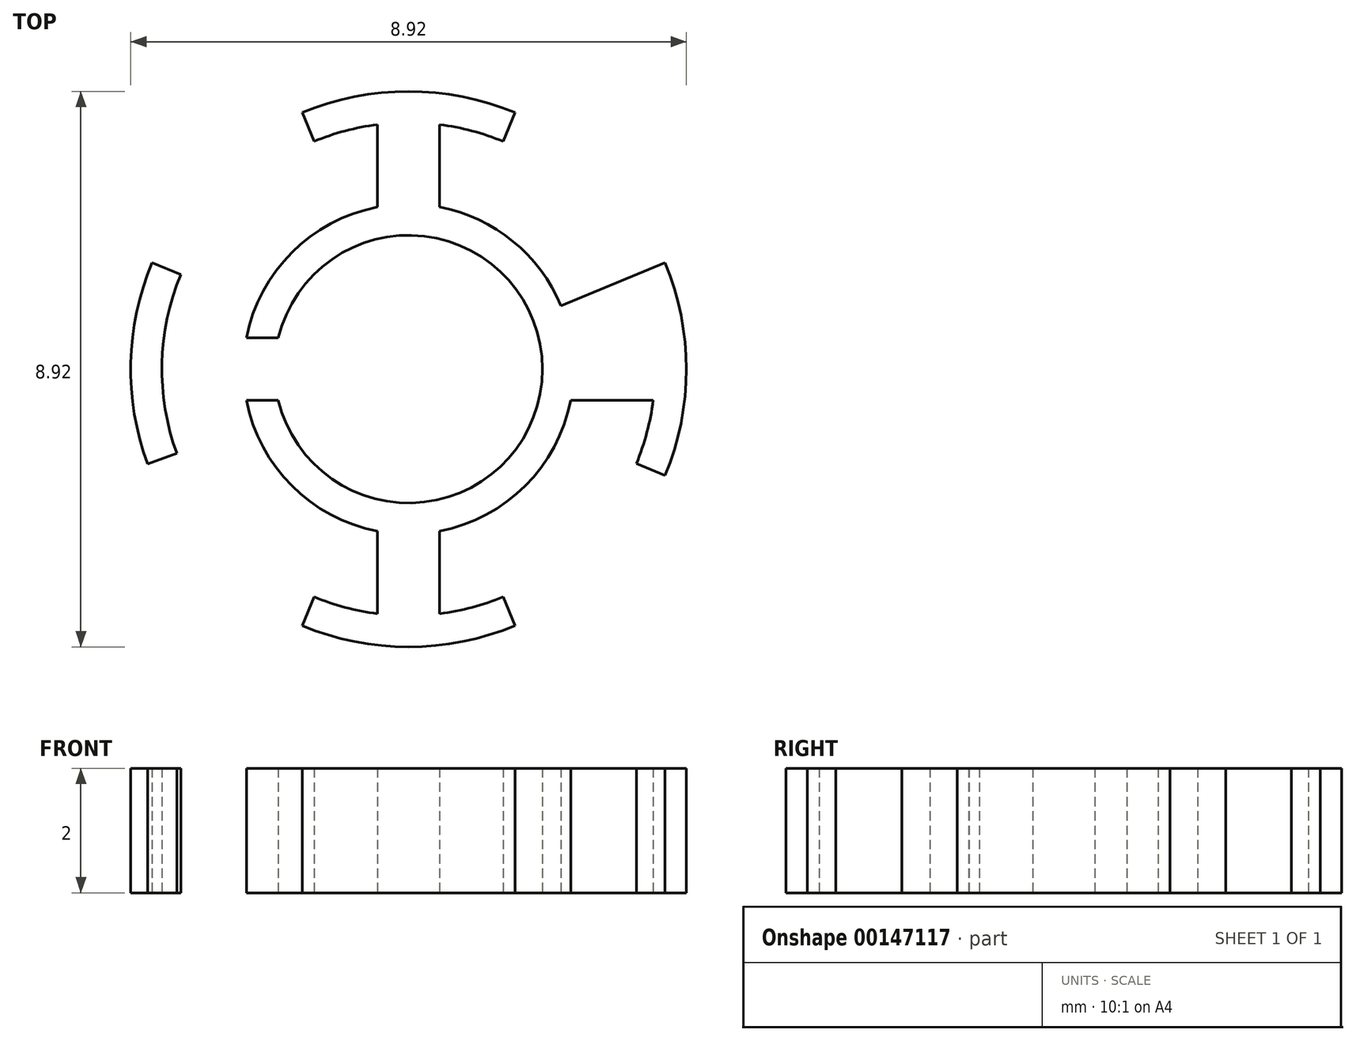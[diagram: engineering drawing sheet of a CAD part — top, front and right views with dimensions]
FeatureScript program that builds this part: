
annotation { "Feature Type Name" : "Feature", "Feature Type Description" : "" }
export const myFeature = defineFeature(function(context is Context, id is Id, definition is map)
    precondition{}
    {
        {
            var Q0;
            Q0=qCreatedBy(makeId("Top.planeOp"),FACE);
            var sketch = newSketch(context, id + "F0", { "sketchPlane" : qUnion([Q0])});
            skCircle(sketch, "E0", {"center": v(0, 0) * mm, "radius": 2.15 * mm});
            skCircle(sketch, "E1", {"center": v(0, 0) * mm, "radius": 2.65 * mm});
            skLineSegment(sketch, "E2", {"start": v(0, 0) * mm, "end": v(0.5, 0) * mm});
            skLineSegment(sketch, "E3", {"start": v(0.5, 0) * mm, "end": v(-0.5, 0) * mm});
            skCircle(sketch, "E4", {"center": v(0, 0) * mm, "radius": 4.46 * mm});
            skCircle(sketch, "E5", {"center": v(0, 0) * mm, "radius": 3.96 * mm});
            skLineSegment(sketch, "E6", {"start": v(-0.5, 0) * mm, "end": v(-0.5, 3.93) * mm});
            skLineSegment(sketch, "E7", {"start": v(0.5, 0) * mm, "end": v(0.5, 3.93) * mm});
            skLineSegment(sketch, "E8", {"start": v(0, 0) * mm, "end": v(0, 4.46) * mm});
            skLineSegment(sketch, "E9", {"start": v(0, 0) * mm, "end": v(1.7, 4.12) * mm});
            skLineSegment(sketch, "E10.MirrorCS", {"start": v(0, 0) * mm, "end": v(-1.7, 4.12) * mm});
            skLineSegment(sketch, "E11.MirrorCS", {"start": v(0, 0) * mm, "end": v(1.7, -4.12) * mm});
            skLineSegment(sketch, "E12.MirrorCS", {"start": v(0, 0) * mm, "end": v(-1.7, -4.12) * mm});
            skLineSegment(sketch, "E13.MirrorCS", {"start": v(0.5, 0) * mm, "end": v(0.5, -3.93) * mm});
            skLineSegment(sketch, "E14.MirrorCS", {"start": v(-0.5, 0) * mm, "end": v(-0.5, -3.93) * mm});
            skLineSegment(sketch, "E15", {"start": v(0, 0) * mm, "end": v(4.12, -1.7) * mm});
            skLineSegment(sketch, "E16", {"start": v(0, 0) * mm, "end": v(4.12, 1.7) * mm});
            skLineSegment(sketch, "E17", {"start": v(0, 0) * mm, "end": v(-4.2, -1.52) * mm});
            skLineSegment(sketch, "E18", {"start": v(0, 0) * mm, "end": v(-4.12, 1.7) * mm});
            skLineSegment(sketch, "E19", {"start": v(0, 0) * mm, "end": v(0, -0.5) * mm});
            skLineSegment(sketch, "E20", {"start": v(0, -0.5) * mm, "end": v(-3.93, -0.5) * mm});
            skLineSegment(sketch, "E21", {"start": v(0, -0.5) * mm, "end": v(0, 0.5) * mm});
            skLineSegment(sketch, "E22", {"start": v(0, 0.5) * mm, "end": v(-3.93, 0.5) * mm});
            skLineSegment(sketch, "E23", {"start": v(-3.93, 0.5) * mm, "end": v(3.93, 0.5) * mm});
            skLineSegment(sketch, "E24", {"start": v(0, -0.5) * mm, "end": v(3.93, -0.5) * mm});
            skSolve(sketch);
        }
        {
            var Q0;
            {var subQ0=sQuery(id+"F0.wireOp",EDGE,"E8");var subQ1=sQuery(id+"F0.wireOp",EDGE,"E4");var subQ2=makeQuery(id+"F0.imprint","INTERSECT",VERTEX,{"derivedFrom":[subQ1,subQ0]});Q0=makeQuery(id+"F0.imprint","IMPRINT",FACE,{"disambiguationData":[TD([[makeQuery(id+"F0.imprint","IMPRINT",EDGE,{"disambiguationData":[TD([[subQ2,1.0]])],"derivedFrom":subQ1}),1.0]])]});}
            var Q1;
            {var subQ0=sQuery(id+"F0.wireOp",EDGE,"E8");var subQ1=sQuery(id+"F0.wireOp",EDGE,"E4");var subQ2=makeQuery(id+"F0.imprint","INTERSECT",VERTEX,{"derivedFrom":[subQ1,subQ0]});Q1=makeQuery(id+"F0.imprint","IMPRINT",FACE,{"disambiguationData":[TD([[makeQuery(id+"F0.imprint","IMPRINT",EDGE,{"disambiguationData":[TD([[subQ2,-1.0]])],"derivedFrom":subQ1}),1.0]])]});}
            var Q2;
            {var subQ0=sQuery(id+"F0.wireOp",EDGE,"E8");var subQ1=sQuery(id+"F0.wireOp",EDGE,"E1");var subQ2=makeQuery(id+"F0.imprint","INTERSECT",VERTEX,{"derivedFrom":[subQ1,subQ0]});Q2=makeQuery(id+"F0.imprint","IMPRINT",FACE,{"disambiguationData":[TD([[makeQuery(id+"F0.imprint","IMPRINT",EDGE,{"disambiguationData":[TD([[subQ2,-1.0]])],"derivedFrom":subQ1}),-1.0]])]});}
            var Q3;
            {var subQ0=sQuery(id+"F0.wireOp",EDGE,"E7");var subQ1=sQuery(id+"F0.wireOp",EDGE,"E1");var subQ2=makeQuery(id+"F0.imprint","INTERSECT",VERTEX,{"derivedFrom":[subQ1,subQ0]});Q3=makeQuery(id+"F0.imprint","IMPRINT",FACE,{"disambiguationData":[TD([[makeQuery(id+"F0.imprint","IMPRINT",EDGE,{"disambiguationData":[TD([[subQ2,-1.0]])],"derivedFrom":subQ1}),-1.0]])]});}
            var Q4;
            {var subQ0=sQuery(id+"F0.wireOp",EDGE,"E7");var subQ1=sQuery(id+"F0.wireOp",EDGE,"E0");var subQ2=makeQuery(id+"F0.imprint","INTERSECT",VERTEX,{"derivedFrom":[subQ1,subQ0]});Q4=makeQuery(id+"F0.imprint","IMPRINT",FACE,{"disambiguationData":[TD([[makeQuery(id+"F0.imprint","IMPRINT",EDGE,{"disambiguationData":[TD([[subQ2,-1.0]])],"derivedFrom":subQ1}),-1.0]])]});}
            var Q5;
            {var subQ0=sQuery(id+"F0.wireOp",EDGE,"E8");var subQ1=sQuery(id+"F0.wireOp",EDGE,"E0");var subQ2=makeQuery(id+"F0.imprint","INTERSECT",VERTEX,{"derivedFrom":[subQ1,subQ0]});Q5=makeQuery(id+"F0.imprint","IMPRINT",FACE,{"disambiguationData":[TD([[makeQuery(id+"F0.imprint","IMPRINT",EDGE,{"disambiguationData":[TD([[subQ2,-1.0]])],"derivedFrom":subQ1}),-1.0]])]});}
            var Q6;
            {var subQ0=sQuery(id+"F0.wireOp",EDGE,"E6");var subQ1=sQuery(id+"F0.wireOp",EDGE,"E0");var subQ2=makeQuery(id+"F0.imprint","INTERSECT",VERTEX,{"derivedFrom":[subQ1,subQ0]});Q6=makeQuery(id+"F0.imprint","IMPRINT",FACE,{"disambiguationData":[TD([[makeQuery(id+"F0.imprint","IMPRINT",EDGE,{"disambiguationData":[TD([[subQ2,-1.0]])],"derivedFrom":subQ1}),-1.0]])]});}
            var Q7;
            {var subQ0=sQuery(id+"F0.wireOp",EDGE,"E7");var subQ1=sQuery(id+"F0.wireOp",EDGE,"E0");var subQ2=makeQuery(id+"F0.imprint","INTERSECT",VERTEX,{"derivedFrom":[subQ1,subQ0]});Q7=makeQuery(id+"F0.imprint","IMPRINT",FACE,{"disambiguationData":[TD([[makeQuery(id+"F0.imprint","IMPRINT",EDGE,{"disambiguationData":[TD([[subQ2,1.0]])],"derivedFrom":subQ1}),-1.0]])]});}
            var Q8;
            {var subQ0=sQuery(id+"F0.wireOp",EDGE,"E9");var subQ1=sQuery(id+"F0.wireOp",EDGE,"E0");var subQ2=makeQuery(id+"F0.imprint","INTERSECT",VERTEX,{"derivedFrom":[subQ1,subQ0]});Q8=makeQuery(id+"F0.imprint","IMPRINT",FACE,{"disambiguationData":[TD([[makeQuery(id+"F0.imprint","IMPRINT",EDGE,{"disambiguationData":[TD([[subQ2,1.0]])],"derivedFrom":subQ1}),-1.0]])]});}
            var Q9;
            {var subQ0=sQuery(id+"F0.wireOp",EDGE,"E10.MirrorCS");var subQ1=sQuery(id+"F0.wireOp",EDGE,"E0");var subQ2=makeQuery(id+"F0.imprint","INTERSECT",VERTEX,{"derivedFrom":[subQ1,subQ0]});Q9=makeQuery(id+"F0.imprint","IMPRINT",FACE,{"disambiguationData":[TD([[makeQuery(id+"F0.imprint","IMPRINT",EDGE,{"disambiguationData":[TD([[subQ2,-1.0]])],"derivedFrom":subQ1}),-1.0]])]});}
            var Q10;
            {var subQ0=sQuery(id+"F0.wireOp",EDGE,"E18");var subQ1=sQuery(id+"F0.wireOp",EDGE,"E0");var subQ2=makeQuery(id+"F0.imprint","INTERSECT",VERTEX,{"derivedFrom":[subQ1,subQ0]});Q10=makeQuery(id+"F0.imprint","IMPRINT",FACE,{"disambiguationData":[TD([[makeQuery(id+"F0.imprint","IMPRINT",EDGE,{"disambiguationData":[TD([[subQ2,-1.0]])],"derivedFrom":subQ1}),-1.0]])]});}
            var Q11;
            {var subQ0=sQuery(id+"F0.wireOp",EDGE,"E23");var subQ1=sQuery(id+"F0.wireOp",EDGE,"E0");var subQ2=makeQuery(id+"F0.imprint","INTERSECT",VERTEX,{"disambiguationData":[OD(1.0)],"derivedFrom":[subQ1,subQ0]});Q11=makeQuery(id+"F0.imprint","IMPRINT",FACE,{"disambiguationData":[TD([[makeQuery(id+"F0.imprint","IMPRINT",EDGE,{"disambiguationData":[TD([[subQ2,-1.0]])],"derivedFrom":subQ1}),-1.0]])]});}
            var Q12;
            {var subQ0=sQuery(id+"F0.wireOp",EDGE,"E20");var subQ1=sQuery(id+"F0.wireOp",EDGE,"E0");var subQ2=makeQuery(id+"F0.imprint","INTERSECT",VERTEX,{"derivedFrom":[subQ1,subQ0]});Q12=makeQuery(id+"F0.imprint","IMPRINT",FACE,{"disambiguationData":[TD([[makeQuery(id+"F0.imprint","IMPRINT",EDGE,{"disambiguationData":[TD([[subQ2,-1.0]])],"derivedFrom":subQ1}),-1.0]])]});}
            var Q13;
            {var subQ0=sQuery(id+"F0.wireOp",EDGE,"E17");var subQ1=sQuery(id+"F0.wireOp",EDGE,"E0");var subQ2=makeQuery(id+"F0.imprint","INTERSECT",VERTEX,{"derivedFrom":[subQ1,subQ0]});Q13=makeQuery(id+"F0.imprint","IMPRINT",FACE,{"disambiguationData":[TD([[makeQuery(id+"F0.imprint","IMPRINT",EDGE,{"disambiguationData":[TD([[subQ2,-1.0]])],"derivedFrom":subQ1}),-1.0]])]});}
            var Q14;
            {var subQ0=sQuery(id+"F0.wireOp",EDGE,"E12.MirrorCS");var subQ1=sQuery(id+"F0.wireOp",EDGE,"E0");var subQ2=makeQuery(id+"F0.imprint","INTERSECT",VERTEX,{"derivedFrom":[subQ1,subQ0]});Q14=makeQuery(id+"F0.imprint","IMPRINT",FACE,{"disambiguationData":[TD([[makeQuery(id+"F0.imprint","IMPRINT",EDGE,{"disambiguationData":[TD([[subQ2,-1.0]])],"derivedFrom":subQ1}),-1.0]])]});}
            var Q15;
            {var subQ0=sQuery(id+"F0.wireOp",EDGE,"E14.MirrorCS");var subQ1=sQuery(id+"F0.wireOp",EDGE,"E0");var subQ2=makeQuery(id+"F0.imprint","INTERSECT",VERTEX,{"derivedFrom":[subQ1,subQ0]});Q15=makeQuery(id+"F0.imprint","IMPRINT",FACE,{"disambiguationData":[TD([[makeQuery(id+"F0.imprint","IMPRINT",EDGE,{"disambiguationData":[TD([[subQ2,-1.0]])],"derivedFrom":subQ1}),-1.0]])]});}
            var Q16;
            {var subQ0=sQuery(id+"F0.wireOp",EDGE,"E13.MirrorCS");var subQ1=sQuery(id+"F0.wireOp",EDGE,"E0");var subQ2=makeQuery(id+"F0.imprint","INTERSECT",VERTEX,{"derivedFrom":[subQ1,subQ0]});Q16=makeQuery(id+"F0.imprint","IMPRINT",FACE,{"disambiguationData":[TD([[makeQuery(id+"F0.imprint","IMPRINT",EDGE,{"disambiguationData":[TD([[subQ2,-1.0]])],"derivedFrom":subQ1}),-1.0]])]});}
            var Q17;
            {var subQ0=sQuery(id+"F0.wireOp",EDGE,"E11.MirrorCS");var subQ1=sQuery(id+"F0.wireOp",EDGE,"E0");var subQ2=makeQuery(id+"F0.imprint","INTERSECT",VERTEX,{"derivedFrom":[subQ1,subQ0]});Q17=makeQuery(id+"F0.imprint","IMPRINT",FACE,{"disambiguationData":[TD([[makeQuery(id+"F0.imprint","IMPRINT",EDGE,{"disambiguationData":[TD([[subQ2,-1.0]])],"derivedFrom":subQ1}),-1.0]])]});}
            var Q18;
            {var subQ0=sQuery(id+"F0.wireOp",EDGE,"E15");var subQ1=sQuery(id+"F0.wireOp",EDGE,"E0");var subQ2=makeQuery(id+"F0.imprint","INTERSECT",VERTEX,{"derivedFrom":[subQ1,subQ0]});Q18=makeQuery(id+"F0.imprint","IMPRINT",FACE,{"disambiguationData":[TD([[makeQuery(id+"F0.imprint","IMPRINT",EDGE,{"disambiguationData":[TD([[subQ2,-1.0]])],"derivedFrom":subQ1}),-1.0]])]});}
            var Q19;
            {var subQ0=sQuery(id+"F0.wireOp",EDGE,"E23");var subQ1=sQuery(id+"F0.wireOp",EDGE,"E0");var subQ2=makeQuery(id+"F0.imprint","INTERSECT",VERTEX,{"disambiguationData":[OD(0.0)],"derivedFrom":[subQ1,subQ0]});Q19=makeQuery(id+"F0.imprint","IMPRINT",FACE,{"disambiguationData":[TD([[makeQuery(id+"F0.imprint","IMPRINT",EDGE,{"disambiguationData":[TD([[subQ2,1.0]])],"derivedFrom":subQ1}),-1.0]])]});}
            var Q20;
            {var subQ0=sQuery(id+"F0.wireOp",EDGE,"E16");var subQ1=sQuery(id+"F0.wireOp",EDGE,"E0");var subQ2=makeQuery(id+"F0.imprint","INTERSECT",VERTEX,{"derivedFrom":[subQ1,subQ0]});Q20=makeQuery(id+"F0.imprint","IMPRINT",FACE,{"disambiguationData":[TD([[makeQuery(id+"F0.imprint","IMPRINT",EDGE,{"disambiguationData":[TD([[subQ2,1.0]])],"derivedFrom":subQ1}),-1.0]])]});}
            var Q21;
            {var subQ0=sQuery(id+"F0.wireOp",EDGE,"E23");var subQ1=sQuery(id+"F0.wireOp",EDGE,"E1");var subQ2=makeQuery(id+"F0.imprint","INTERSECT",VERTEX,{"disambiguationData":[OD(0.0)],"derivedFrom":[subQ1,subQ0]});Q21=makeQuery(id+"F0.imprint","IMPRINT",FACE,{"disambiguationData":[TD([[makeQuery(id+"F0.imprint","IMPRINT",EDGE,{"disambiguationData":[TD([[subQ2,1.0]])],"derivedFrom":subQ1}),-1.0]])]});}
            var Q22;
            {var subQ3=sQuery(id+"F0.wireOp",EDGE,"E15");var subQ4=sQuery(id+"F0.wireOp",EDGE,"E4");var subQ5=makeQuery(id+"F0.imprint","INTERSECT",VERTEX,{"derivedFrom":[subQ4,subQ3]});Q22=makeQuery(id+"F0.imprint","IMPRINT",FACE,{"disambiguationData":[TD([[makeQuery(id+"F0.imprint","IMPRINT",EDGE,{"disambiguationData":[TD([[subQ5,-1.0]])],"derivedFrom":subQ4}),1.0]])]});}
            var Q23;
            {var subQ0=sQuery(id+"F0.wireOp",EDGE,"E23");var subQ1=sQuery(id+"F0.wireOp",EDGE,"E1");var subQ2=makeQuery(id+"F0.imprint","INTERSECT",VERTEX,{"disambiguationData":[OD(1.0)],"derivedFrom":[subQ1,subQ0]});Q23=makeQuery(id+"F0.imprint","IMPRINT",FACE,{"disambiguationData":[TD([[makeQuery(id+"F0.imprint","IMPRINT",EDGE,{"disambiguationData":[TD([[subQ2,-1.0]])],"derivedFrom":subQ1}),-1.0]])]});}
            var Q24;
            {var subQ2=sQuery(id+"F0.wireOp",EDGE,"E17");var subQ4=sQuery(id+"F0.wireOp",EDGE,"E4");var subQ5=makeQuery(id+"F0.imprint","INTERSECT",VERTEX,{"derivedFrom":[subQ4,subQ2]});Q24=makeQuery(id+"F0.imprint","IMPRINT",FACE,{"disambiguationData":[TD([[makeQuery(id+"F0.imprint","IMPRINT",EDGE,{"disambiguationData":[TD([[subQ5,1.0]])],"derivedFrom":subQ4}),1.0]])]});}
            var Q25;
            {var subQ0=sQuery(id+"F0.wireOp",EDGE,"E14.MirrorCS");var subQ1=sQuery(id+"F0.wireOp",EDGE,"E1");var subQ2=makeQuery(id+"F0.imprint","INTERSECT",VERTEX,{"derivedFrom":[subQ1,subQ0]});Q25=makeQuery(id+"F0.imprint","IMPRINT",FACE,{"disambiguationData":[TD([[makeQuery(id+"F0.imprint","IMPRINT",EDGE,{"disambiguationData":[TD([[subQ2,-1.0]])],"derivedFrom":subQ1}),-1.0]])]});}
            var Q26;
            {var subQ4=sQuery(id+"F0.wireOp",EDGE,"E4");var subQ7=sQuery(id+"F0.wireOp",EDGE,"E11.MirrorCS");var subQ9=makeQuery(id+"F0.imprint","INTERSECT",VERTEX,{"derivedFrom":[subQ4,subQ7]});Q26=makeQuery(id+"F0.imprint","IMPRINT",FACE,{"disambiguationData":[TD([[makeQuery(id+"F0.imprint","IMPRINT",EDGE,{"disambiguationData":[TD([[subQ9,1.0]])],"derivedFrom":subQ4}),1.0]])]});}
            extrude(context, id + "F1", {"entities" : qUnion([Q0, Q1, Q2, Q3, Q4, Q5, Q6, Q7, Q8, Q9, Q10, Q11, Q12, Q13, Q14, Q15, Q16, Q17, Q18, Q19, Q20, Q21, Q22, Q23, Q24, Q25, Q26]), "depth" : 2 * mm});
        }
    });
